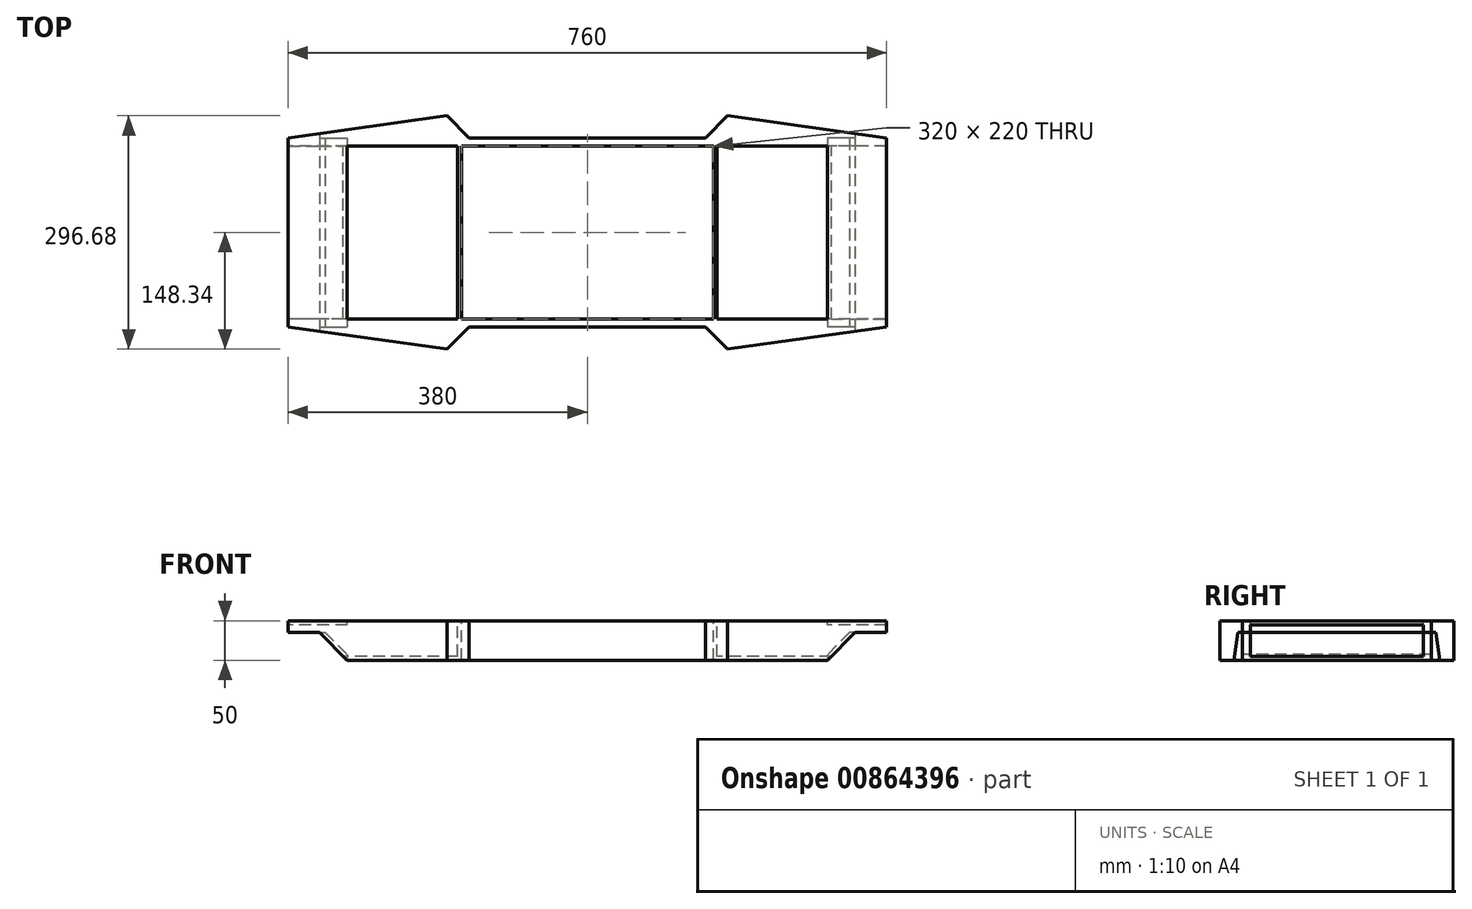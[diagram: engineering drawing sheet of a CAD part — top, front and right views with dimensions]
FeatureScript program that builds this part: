
annotation { "Feature Type Name" : "Feature", "Feature Type Description" : "" }
export const myFeature = defineFeature(function(context is Context, id is Id, definition is map)
    precondition{}
    {
        {
            var Q0;
            Q0=qCreatedBy(makeId("Top.planeOp"),FACE);
            var sketch = newSketch(context, id + "F0", { "sketchPlane" : qUnion([Q0])});
            skLineSegment(sketch, "E0", {"start": v(-380, 120) * mm, "end": v(-380, -120) * mm});
            skLineSegment(sketch, "E1", {"start": v(380, 120) * mm, "end": v(380, -120) * mm});
            skLineSegment(sketch, "E2", {"start": v(150, -120) * mm, "end": v(-150, -120) * mm});
            skLineSegment(sketch, "E3", {"start": v(-150, 120) * mm, "end": v(150, 120) * mm});
            skLineSegment(sketch, "E4", {"start": v(-160, 110) * mm, "end": v(160, 110) * mm, "construction": true});
            skLineSegment(sketch, "E5", {"start": v(160, 110) * mm, "end": v(160, -110) * mm, "construction": true});
            skLineSegment(sketch, "E6", {"start": v(160, -110) * mm, "end": v(-160, -110) * mm, "construction": true});
            skLineSegment(sketch, "E7", {"start": v(-160, -110) * mm, "end": v(-160, 110) * mm, "construction": true});
            skLineSegment(sketch, "E8.0", {"start": v(-150, -110) * mm, "end": v(-150, 110) * mm, "construction": true});
            skLineSegment(sketch, "E9.0", {"start": v(150, 110) * mm, "end": v(150, -110) * mm, "construction": true});
            skLineSegment(sketch, "E10", {"start": v(-150, -110) * mm, "end": v(-150, -120) * mm, "construction": true});
            skLineSegment(sketch, "E11", {"start": v(-150, 110) * mm, "end": v(-150, 120) * mm, "construction": true});
            skLineSegment(sketch, "E12", {"start": v(-150, 120) * mm, "end": v(-178.34, 148.34) * mm});
            skLineSegment(sketch, "E13", {"start": v(-380, 120) * mm, "end": v(-178.34, 148.34) * mm});
            skPoint(sketch, "E14.endSnap0", {"position": v(0, 110) * mm});
            skLineSegment(sketch, "E15.MirrorCS", {"start": v(150, 120) * mm, "end": v(178.34, 148.34) * mm});
            skLineSegment(sketch, "E16.MirrorCS", {"start": v(380, 120) * mm, "end": v(178.34, 148.34) * mm});
            skLineSegment(sketch, "E17.MirrorCS", {"start": v(-150, -120) * mm, "end": v(-178.34, -148.34) * mm, "construction": true});
            skLineSegment(sketch, "E18.MirrorCS", {"start": v(-380, -120) * mm, "end": v(-178.34, -148.34) * mm});
            skLineSegment(sketch, "E19.MirrorCS", {"start": v(150, -120) * mm, "end": v(178.34, -148.34) * mm});
            skLineSegment(sketch, "E20.MirrorCS", {"start": v(-150, -120) * mm, "end": v(-178.34, -148.34) * mm});
            skLineSegment(sketch, "E21.MirrorCS", {"start": v(380, -120) * mm, "end": v(178.34, -148.34) * mm});
            skSolve(sketch);
        }
        {
            var Q0;
            Q0=makeQuery(id+"F0.imprint","IMPRINT",FACE,{"disambiguationData":[TD([[makeQuery(id+"F0.imprint","IMPRINT",EDGE,{"derivedFrom":sQuery(id+"F0.wireOp",EDGE,"E0")}),1.0]])]});
            extrude(context, id + "F1", {"entities" : qUnion([Q0]), "depth" : 50 * mm, "offsetDistance" : 25 * mm});
        }
        {
            var Q0;
            Q0=makeQuery(id+"F1.opExtrude","SWEPT_FACE",FACE,{"disambiguationData":[OSD([sQuery(id+"F0.wireOp",EDGE,"E2")])]});
            var sketch = newSketch(context, id + "F2", { "sketchPlane" : qUnion([Q0])});
            skLineSegment(sketch, "E22", {"start": v(-380, 35) * mm, "end": v(-340, 35) * mm});
            skLineSegment(sketch, "E23", {"start": v(-340, 35) * mm, "end": v(-305, 0) * mm});
            skLineSegment(sketch, "E24", {"start": v(-380, 35) * mm, "end": v(-380, 0) * mm});
            skLineSegment(sketch, "E25", {"start": v(-380, 0) * mm, "end": v(-305, 0) * mm});
            skLineSegment(sketch, "E26.MirrorCS", {"start": v(380, 0) * mm, "end": v(305, 0) * mm});
            skLineSegment(sketch, "E27.MirrorCS", {"start": v(380, 35) * mm, "end": v(380, 0) * mm});
            skLineSegment(sketch, "E28.MirrorCS", {"start": v(380, 35) * mm, "end": v(340, 35) * mm});
            skLineSegment(sketch, "E29.MirrorCS", {"start": v(340, 35) * mm, "end": v(305, 0) * mm});
            skSolve(sketch);
        }
        {
            var Q0;
            Q0=makeQuery(id+"F1.opExtrude","SWEPT_FACE",FACE,{"disambiguationData":[OSD([sQuery(id+"F0.wireOp",EDGE,"E0")])]});
            var sketch = newSketch(context, id + "F3", { "sketchPlane" : qUnion([Q0])});
            skLineSegment(sketch, "E30.0", {"start": v(-110, 45) * mm, "end": v(110, 45) * mm});
            skLineSegment(sketch, "E31.0", {"start": v(-110, 5) * mm, "end": v(110, 5) * mm});
            skLineSegment(sketch, "E32.0", {"start": v(-110, 5) * mm, "end": v(-110, 45) * mm});
            skLineSegment(sketch, "E33.0", {"start": v(110, 45) * mm, "end": v(110, 5) * mm});
            skSolve(sketch);
        }
        {
            var Q0;
            Q0=makeQuery(id+"F3.imprint","IMPRINT",FACE,{"disambiguationData":[TD([[makeQuery(id+"F3.imprint","IMPRINT",EDGE,{"derivedFrom":sQuery(id+"F3.wireOp",EDGE,"E30.0")}),-1.0]])]});
            extrude(context, id + "F4", {"entities" : qUnion([Q0]), "operationType" : NewBodyOperationType.REMOVE, "oppositeDirection" : true, "depth" : 760 * mm, "offsetDistance" : 25 * mm});
        }
        {
            var Q0;
            Q0=makeQuery(id+"F2.imprint","IMPRINT",FACE,{"disambiguationData":[TD([[makeQuery(id+"F2.imprint","IMPRINT",EDGE,{"derivedFrom":sQuery(id+"F2.wireOp",EDGE,"E26.MirrorCS")}),-1.0]])]});
            var Q1;
            Q1=makeQuery(id+"F2.imprint","IMPRINT",FACE,{"disambiguationData":[TD([[makeQuery(id+"F2.imprint","IMPRINT",EDGE,{"derivedFrom":sQuery(id+"F2.wireOp",EDGE,"E22")}),-1.0]])]});
            extrude(context, id + "F5", {"entities" : qUnion([Q0, Q1]), "operationType" : NewBodyOperationType.REMOVE, "oppositeDirection" : true, "depth" : 240 * mm, "offsetDistance" : 25 * mm});
        }
        {
            var Q0;
            Q0=makeQuery(id+"F1.opExtrude","CAP_FACE",FACE,{"disambiguationData":[OSD([sQuery(id+"F0.wireOp",EDGE,"E0"),sQuery(id+"F0.wireOp",EDGE,"E1"),sQuery(id+"F0.wireOp",EDGE,"E2"),sQuery(id+"F0.wireOp",EDGE,"E3")])],"isStart":false});
            var sketch = newSketch(context, id + "F6", { "sketchPlane" : qUnion([Q0])});
            skLineSegment(sketch, "E34", {"start": v(-140, 90) * mm, "end": v(140, 90) * mm});
            skLineSegment(sketch, "E35", {"start": v(140, 90) * mm, "end": v(140, -90) * mm});
            skLineSegment(sketch, "E36", {"start": v(140, -90) * mm, "end": v(-140, -90) * mm});
            skLineSegment(sketch, "E37", {"start": v(-140, -90) * mm, "end": v(-140, 90) * mm});
            skLineSegment(sketch, "E38", {"start": v(160, 110) * mm, "end": v(160, -110) * mm});
            skLineSegment(sketch, "E39", {"start": v(-160, 110) * mm, "end": v(-160, -110) * mm});
            skLineSegment(sketch, "E40", {"start": v(-160, 110) * mm, "end": v(160, 110) * mm});
            skLineSegment(sketch, "E41", {"start": v(160, -110) * mm, "end": v(-160, -110) * mm});
            skSolve(sketch);
        }
        {
            var Q0;
            Q0=qSketchRegion(id+"F6",true);
            extrude(context, id + "F7", {"entities" : qUnion([Q0]), "operationType" : NewBodyOperationType.REMOVE, "oppositeDirection" : true, "depth" : 50 * mm, "offsetDistance" : 25 * mm});
        }
        {
            var Q0;
            Q0=qSketchRegion(id+"F2",true);
            extrude(context, id + "F8", {"entities" : qUnion([Q0]), "operationType" : NewBodyOperationType.REMOVE, "endBound" : BoundingType.SYMMETRIC, "oppositeDirection" : true, "depth" : 871.86 * mm, "offsetDistance" : 25 * mm});
        }
        {
            var Q0;
            {var subQ0=sQuery(id+"F0.wireOp",EDGE,"E18.MirrorCS");var subQ1=sQuery(id+"F0.wireOp",EDGE,"E16.MirrorCS");var subQ2=sQuery(id+"F0.wireOp",EDGE,"E15.MirrorCS");var subQ3=sQuery(id+"F0.wireOp",EDGE,"E13");var subQ4=sQuery(id+"F0.wireOp",EDGE,"E12");var subQ5=sQuery(id+"F0.wireOp",EDGE,"E19.MirrorCS");var subQ6=sQuery(id+"F0.wireOp",EDGE,"E0");var subQ7=sQuery(id+"F0.wireOp",EDGE,"E3");var subQ8=sQuery(id+"F0.wireOp",EDGE,"E1");var subQ9=sQuery(id+"F0.wireOp",EDGE,"E2");var subQ10=sQuery(id+"F0.wireOp",EDGE,"E20.MirrorCS");var subQ11=sQuery(id+"F0.wireOp",EDGE,"E21.MirrorCS");Q0=makeQuery(id+"F7.boolean.opBoolean","SPLIT",FACE,{"disambiguationData":[TD([makeQuery(id+"F1.opExtrude","SWEPT_FACE",FACE,{"disambiguationData":[OSD([subQ6])]})])],"derivedFrom":makeQuery(id+"F1.opExtrude","CAP_FACE",FACE,{"disambiguationData":[OSD([subQ6,subQ8,subQ9,subQ7,subQ4,subQ3,subQ2,subQ1,subQ0,subQ5,subQ10,subQ11])],"isStart":false})});}
            var sketch = newSketch(context, id + "F9", { "sketchPlane" : qUnion([Q0])});
            skLineSegment(sketch, "E42", {"start": v(-165, -110) * mm, "end": v(-305, -110) * mm});
            skLineSegment(sketch, "E43", {"start": v(-305, -110) * mm, "end": v(-305, 110) * mm});
            skLineSegment(sketch, "E44", {"start": v(-305, 110) * mm, "end": v(-165, 110) * mm});
            skLineSegment(sketch, "E45.0", {"start": v(-165, 110) * mm, "end": v(-165, -110) * mm});
            skLineSegment(sketch, "E46", {"start": v(0, 0) * mm, "end": v(0, 58.76) * mm});
            skLineSegment(sketch, "E47.MirrorCS", {"start": v(165, 110) * mm, "end": v(165, -110) * mm});
            skLineSegment(sketch, "E48.MirrorCS", {"start": v(165, -110) * mm, "end": v(305, -110) * mm});
            skLineSegment(sketch, "E49.MirrorCS", {"start": v(305, -110) * mm, "end": v(305, 110) * mm});
            skLineSegment(sketch, "E50.MirrorCS", {"start": v(305, 110) * mm, "end": v(165, 110) * mm});
            skSolve(sketch);
        }
        {
            var Q0;
            Q0=makeQuery(id+"F9.imprint","IMPRINT",FACE,{"disambiguationData":[TD([[makeQuery(id+"F9.imprint","IMPRINT",EDGE,{"derivedFrom":sQuery(id+"F9.wireOp",EDGE,"E42")}),-1.0]])]});
            var Q1;
            Q1=makeQuery(id+"F9.imprint","IMPRINT",FACE,{"disambiguationData":[TD([[makeQuery(id+"F9.imprint","IMPRINT",EDGE,{"derivedFrom":sQuery(id+"F9.wireOp",EDGE,"E47.MirrorCS")}),1.0]])]});
            extrude(context, id + "F10", {"entities" : qUnion([Q0, Q1]), "operationType" : NewBodyOperationType.REMOVE, "oppositeDirection" : true, "depth" : 10 * mm, "offsetDistance" : 25 * mm});
        }
        {
            var Q0;
            Q0=makeQuery(id+"F1.opExtrude","SWEPT_FACE",FACE,{"disambiguationData":[OSD([sQuery(id+"F0.wireOp",EDGE,"E2")])]});
            var sketch = newSketch(context, id + "F11", { "sketchPlane" : qUnion([Q0])});
            skLineSegment(sketch, "E51", {"start": v(-305, 50) * mm, "end": v(-305, 0) * mm});
            skLineSegment(sketch, "E52", {"start": v(-340, 50) * mm, "end": v(-340, 35) * mm});
            skLineSegment(sketch, "E53", {"start": v(-340, 35) * mm, "end": v(-305, 0) * mm});
            skLineSegment(sketch, "E54.0", {"start": v(-332.93, 35) * mm, "end": v(-305, 7.07) * mm});
            skLineSegment(sketch, "E55", {"start": v(-340, 35) * mm, "end": v(-332.93, 35) * mm});
            skLineSegment(sketch, "E56", {"start": v(0, 0) * mm, "end": v(0, 50) * mm});
            skLineSegment(sketch, "E57", {"start": v(-340, 35) * mm, "end": v(-346.55, 35) * mm});
            skLineSegment(sketch, "E58.MirrorCS", {"start": v(332.93, 35) * mm, "end": v(305, 7.07) * mm});
            skLineSegment(sketch, "E59.MirrorCS", {"start": v(340, 35) * mm, "end": v(305, 0) * mm});
            skLineSegment(sketch, "E60.MirrorCS", {"start": v(340, 35) * mm, "end": v(332.93, 35) * mm});
            skLineSegment(sketch, "E61", {"start": v(305, 7.07) * mm, "end": v(305, 0) * mm});
            skSolve(sketch);
        }
        {
            var Q0;
            {var subQ0=sQuery(id+"F11.wireOp",EDGE,"E53");Q0=makeQuery(id+"F11.imprint","IMPRINT",FACE,{"disambiguationData":[TD([[makeQuery(id+"F11.imprint","IMPRINT",EDGE,{"derivedFrom":subQ0}),1.0]])]});}
            var Q1;
            Q1=makeQuery(id+"F11.imprint","IMPRINT",FACE,{"disambiguationData":[TD([[makeQuery(id+"F11.imprint","IMPRINT",EDGE,{"derivedFrom":sQuery(id+"F11.wireOp",EDGE,"E58.MirrorCS")}),1.0]])]});
            extrude(context, id + "F12", {"entities" : qUnion([Q0, Q1]), "oppositeDirection" : true, "depth" : 240 * mm, "offsetDistance" : 25 * mm});
        }
        {
            var Q0;
            Q0=makeQuery(id+"F7.boolean.opBoolean","SPLIT",FACE,{"disambiguationData":[TD([makeQuery(id+"F7.opExtrude","SWEPT_FACE",FACE,{"disambiguationData":[OSD([sQuery(id+"F6.wireOp",EDGE,"E34")])]})])],"derivedFrom":makeQuery(id+"F1.opExtrude","CAP_FACE",FACE,{"disambiguationData":[OSD([sQuery(id+"F0.wireOp",EDGE,"E0"),sQuery(id+"F0.wireOp",EDGE,"E1"),sQuery(id+"F0.wireOp",EDGE,"E2"),sQuery(id+"F0.wireOp",EDGE,"E3"),sQuery(id+"F0.wireOp",EDGE,"E12"),sQuery(id+"F0.wireOp",EDGE,"E13"),sQuery(id+"F0.wireOp",EDGE,"E15.MirrorCS"),sQuery(id+"F0.wireOp",EDGE,"E16.MirrorCS"),sQuery(id+"F0.wireOp",EDGE,"E18.MirrorCS"),sQuery(id+"F0.wireOp",EDGE,"E19.MirrorCS"),sQuery(id+"F0.wireOp",EDGE,"E20.MirrorCS"),sQuery(id+"F0.wireOp",EDGE,"E21.MirrorCS")])],"isStart":false})});
            extrude(context, id + "F13", {"entities" : qUnion([Q0]), "operationType" : NewBodyOperationType.REMOVE, "oppositeDirection" : true, "depth" : 25 * mm, "offsetDistance" : 25 * mm});
        }
        {
            var Q0;
            Q0=makeQuery(id+"F7.boolean.opBoolean","SPLIT",FACE,{"disambiguationData":[TD([makeQuery(id+"F7.opExtrude","SWEPT_FACE",FACE,{"disambiguationData":[OSD([sQuery(id+"F6.wireOp",EDGE,"E34")])]})])],"derivedFrom":makeQuery(id+"F1.opExtrude","CAP_FACE",FACE,{"disambiguationData":[OSD([sQuery(id+"F0.wireOp",EDGE,"E0"),sQuery(id+"F0.wireOp",EDGE,"E1"),sQuery(id+"F0.wireOp",EDGE,"E2"),sQuery(id+"F0.wireOp",EDGE,"E3"),sQuery(id+"F0.wireOp",EDGE,"E12"),sQuery(id+"F0.wireOp",EDGE,"E13"),sQuery(id+"F0.wireOp",EDGE,"E15.MirrorCS"),sQuery(id+"F0.wireOp",EDGE,"E16.MirrorCS"),sQuery(id+"F0.wireOp",EDGE,"E18.MirrorCS"),sQuery(id+"F0.wireOp",EDGE,"E19.MirrorCS"),sQuery(id+"F0.wireOp",EDGE,"E20.MirrorCS"),sQuery(id+"F0.wireOp",EDGE,"E21.MirrorCS")])],"isStart":true})});
            extrude(context, id + "F14", {"entities" : qUnion([Q0]), "operationType" : NewBodyOperationType.REMOVE, "oppositeDirection" : true, "depth" : 25 * mm, "offsetDistance" : 25 * mm});
        }
        {
            var Q0;
            Q0=makeQuery(id+"F7.boolean.opBoolean","COPY",FACE,{"disambiguationData":[TD([makeQuery(id+"F4.boolean.opBoolean","COPY",FACE,{"derivedFrom":makeQuery(id+"F4.opExtrude","SWEPT_FACE",FACE,{"disambiguationData":[OSD([sQuery(id+"F3.wireOp",EDGE,"E30.0")])]})})])],"derivedFrom":makeQuery(id+"F7.opExtrude","SWEPT_FACE",FACE,{"disambiguationData":[OSD([sQuery(id+"F6.wireOp",EDGE,"E38")])]})});
            var sketch = newSketch(context, id + "F15", { "sketchPlane" : qUnion([Q0])});
            skLineSegment(sketch, "E62", {"start": v(-110, 45) * mm, "end": v(-110, 5) * mm});
            skLineSegment(sketch, "E63", {"start": v(-110, 45) * mm, "end": v(110, 45) * mm});
            skLineSegment(sketch, "E64", {"start": v(110, 45) * mm, "end": v(110, 5) * mm});
            skLineSegment(sketch, "E65", {"start": v(-110, 5) * mm, "end": v(110, 5) * mm});
            skSolve(sketch);
        }
        {
            var Q0;
            Q0=makeQuery(id+"F7.boolean.opBoolean","COPY",FACE,{"disambiguationData":[TD([makeQuery(id+"F4.boolean.opBoolean","COPY",FACE,{"derivedFrom":makeQuery(id+"F4.opExtrude","SWEPT_FACE",FACE,{"disambiguationData":[OSD([sQuery(id+"F3.wireOp",EDGE,"E31.0")])]})})])],"derivedFrom":makeQuery(id+"F7.opExtrude","SWEPT_FACE",FACE,{"disambiguationData":[OSD([sQuery(id+"F6.wireOp",EDGE,"E39")])]})});
            var sketch = newSketch(context, id + "F16", { "sketchPlane" : qUnion([Q0])});
            skLineSegment(sketch, "E66", {"start": v(-110, 5) * mm, "end": v(-110, 45) * mm});
            skLineSegment(sketch, "E67", {"start": v(-110, 5) * mm, "end": v(110, 5) * mm});
            skLineSegment(sketch, "E68", {"start": v(110, 5) * mm, "end": v(110, 45) * mm});
            skLineSegment(sketch, "E69", {"start": v(-110, 45) * mm, "end": v(110, 45) * mm});
            skSolve(sketch);
        }
        {
            var Q0;
            Q0=qSketchRegion(id+"F16",true);
            extrude(context, id + "F17", {"entities" : qUnion([Q0]), "operationType" : NewBodyOperationType.ADD, "oppositeDirection" : true, "depth" : 5 * mm, "offsetDistance" : 25 * mm});
        }
        {
            var Q0;
            Q0=makeQuery(id+"F15.imprint","IMPRINT",FACE,{"disambiguationData":[TD([[makeQuery(id+"F15.imprint","IMPRINT",EDGE,{"derivedFrom":sQuery(id+"F15.wireOp",EDGE,"E62")}),1.0]])]});
            extrude(context, id + "F18", {"entities" : qUnion([Q0]), "operationType" : NewBodyOperationType.ADD, "oppositeDirection" : true, "depth" : 5 * mm, "offsetDistance" : 25 * mm});
        }
    });
